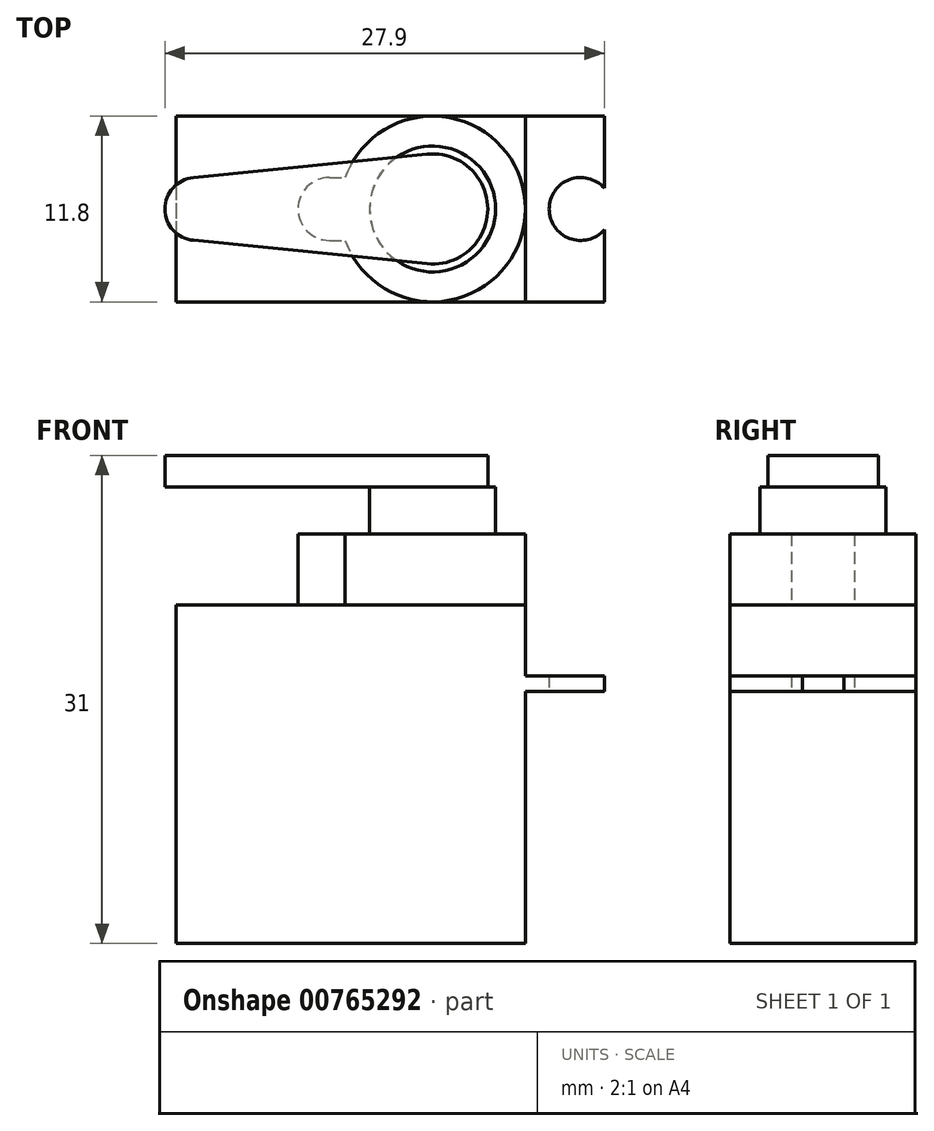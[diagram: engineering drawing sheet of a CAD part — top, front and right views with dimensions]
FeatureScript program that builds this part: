
annotation { "Feature Type Name" : "Feature", "Feature Type Description" : "" }
export const myFeature = defineFeature(function(context is Context, id is Id, definition is map)
    precondition{}
    {
        {
            var Q0;
            Q0=qCreatedBy(makeId("Top.planeOp"),FACE);
            var sketch = newSketch(context, id + "F0", { "sketchPlane" : qUnion([Q0])});
            skLineSegment(sketch, "E0.bottom", {"start": v(11.1, 5.9) * mm, "end": v(-11.1, 5.9) * mm});
            skLineSegment(sketch, "E0.top", {"start": v(11.1, -5.9) * mm, "end": v(-11.1, -5.9) * mm});
            skLineSegment(sketch, "E0.left", {"start": v(11.1, 5.9) * mm, "end": v(11.1, -5.9) * mm});
            skLineSegment(sketch, "E0.right", {"start": v(-11.1, 5.9) * mm, "end": v(-11.1, -5.9) * mm});
            skPoint(sketch, "E0.middle", {"position": v(0, 0) * mm});
            skSolve(sketch);
        }
        {
            var Q0;
            Q0=qSketchRegion(id+"F0",true);
            extrude(context, id + "F1", {"entities" : qUnion([Q0]), "depth" : 21.5 * mm});
        }
        {
            var Q0;
            Q0=qCreatedBy(makeId("Top.planeOp"),FACE);
            cPlane(context, id + "F2", {"entities" : qUnion([Q0]), "cplaneType" : CPlaneType.OFFSET, "offset" : 16 * mm, "width" : 150 * mm, "height" : 150 * mm});
        }
        {
            var Q0;
            Q0=qCreatedBy(id+"F2.planeOp",FACE);
            var sketch = newSketch(context, id + "F3", { "sketchPlane" : qUnion([Q0])});
            skLineSegment(sketch, "E1.0", {"start": v(-11.1, 5.9) * mm, "end": v(-11.1, -5.9) * mm});
            skLineSegment(sketch, "E2.0", {"start": v(11.1, 5.9) * mm, "end": v(11.1, -5.9) * mm});
            skLineSegment(sketch, "E3.bottom", {"start": v(11.1, 5.9) * mm, "end": v(16.1, 5.9) * mm});
            skLineSegment(sketch, "E3.top", {"start": v(11.1, -5.9) * mm, "end": v(16.1, -5.9) * mm});
            skLineSegment(sketch, "E3.right", {"start": v(16.1, 5.9) * mm, "end": v(16.1, -5.9) * mm});
            skCircle(sketch, "E4", {"center": v(14.6, 0) * mm, "radius": 2 * mm});
            skPoint(sketch, "E4.centerSnap0", {"position": v(16.1, 0) * mm});
            skSolve(sketch);
        }
        {
            var Q0;
            Q0=makeQuery(id+"F1.opExtrude","CAP_FACE",FACE,{"disambiguationData":[OSD([sQuery(id+"F0.wireOp",EDGE,"E0.bottom"),sQuery(id+"F0.wireOp",EDGE,"E0.top"),sQuery(id+"F0.wireOp",EDGE,"E0.left"),sQuery(id+"F0.wireOp",EDGE,"E0.right")])],"isStart":false});
            var sketch = newSketch(context, id + "F4", { "sketchPlane" : qUnion([Q0])});
            skArc(sketch, "E5", {"start": v(-0.35, -2) * mm, "mid": v(11.1, 0) * mm, "end": v(-0.35, 2) * mm});
            skArc(sketch, "E6", {"start": v(-1.35, 2) * mm, "mid": v(-3.35, 0) * mm, "end": v(-1.35, -2) * mm});
            skLineSegment(sketch, "E7", {"start": v(-1.35, 2) * mm, "end": v(-0.35, 2) * mm});
            skLineSegment(sketch, "E8", {"start": v(-1.35, -2) * mm, "end": v(-0.35, -2) * mm});
            skSolve(sketch);
        }
        {
            var Q0;
            Q0=qSketchRegion(id+"F4",true);
            extrude(context, id + "F5", {"entities" : qUnion([Q0]), "operationType" : NewBodyOperationType.ADD, "depth" : 4.5 * mm});
        }
        {
            var Q0;
            {var subQ1=sQuery(id+"F3.wireOp",EDGE,"E3.bottom");Q0=makeQuery(id+"F3.imprint","IMPRINT",FACE,{"disambiguationData":[TD([[makeQuery(id+"F3.imprint","IMPRINT",EDGE,{"derivedFrom":subQ1}),-1.0]])]});}
            extrude(context, id + "F6", {"entities" : qUnion([Q0]), "operationType" : NewBodyOperationType.ADD, "depth" : 1 * mm});
        }
        {
            var Q0;
            Q0=makeQuery(id+"F5.opExtrude","CAP_FACE",FACE,{"disambiguationData":[OSD([sQuery(id+"F4.wireOp",EDGE,"E5"),sQuery(id+"F4.wireOp",EDGE,"E6"),sQuery(id+"F4.wireOp",EDGE,"E7"),sQuery(id+"F4.wireOp",EDGE,"E8")])],"isStart":false});
            var sketch = newSketch(context, id + "F7", { "sketchPlane" : qUnion([Q0])});
            skCircle(sketch, "E9", {"center": v(5.2, 0) * mm, "radius": 4 * mm});
            skSolve(sketch);
        }
        {
            var Q0;
            Q0=qSketchRegion(id+"F7",true);
            extrude(context, id + "F8", {"entities" : qUnion([Q0]), "depth" : 3 * mm});
        }
        {
            var Q0;
            Q0=makeQuery(id+"F8.opExtrude","CAP_FACE",FACE,{"disambiguationData":[OSD([sQuery(id+"F7.wireOp",EDGE,"E9")])],"isStart":false});
            var sketch = newSketch(context, id + "F9", { "sketchPlane" : qUnion([Q0])});
            skCircle(sketch, "E10", {"center": v(5.2, 0) * mm, "radius": 3.5 * mm});
            skLineSegment(sketch, "E11", {"start": v(5.2, 0) * mm, "end": v(-9.8, 0) * mm, "construction": true});
            skArc(sketch, "E12", {"start": v(-10, 1.99) * mm, "mid": v(-11.8, 0) * mm, "end": v(-10, -1.99) * mm});
            skLineSegment(sketch, "E13", {"start": v(4.85, 3.48) * mm, "end": v(-10, 1.99) * mm});
            skLineSegment(sketch, "E14", {"start": v(-10, -1.99) * mm, "end": v(4.85, -3.48) * mm});
            skSolve(sketch);
        }
        {
            var Q0;
            Q0=qSketchRegion(id+"F9",true);
            extrude(context, id + "F10", {"entities" : qUnion([Q0]), "operationType" : NewBodyOperationType.ADD, "depth" : 2 * mm});
        }
    });
